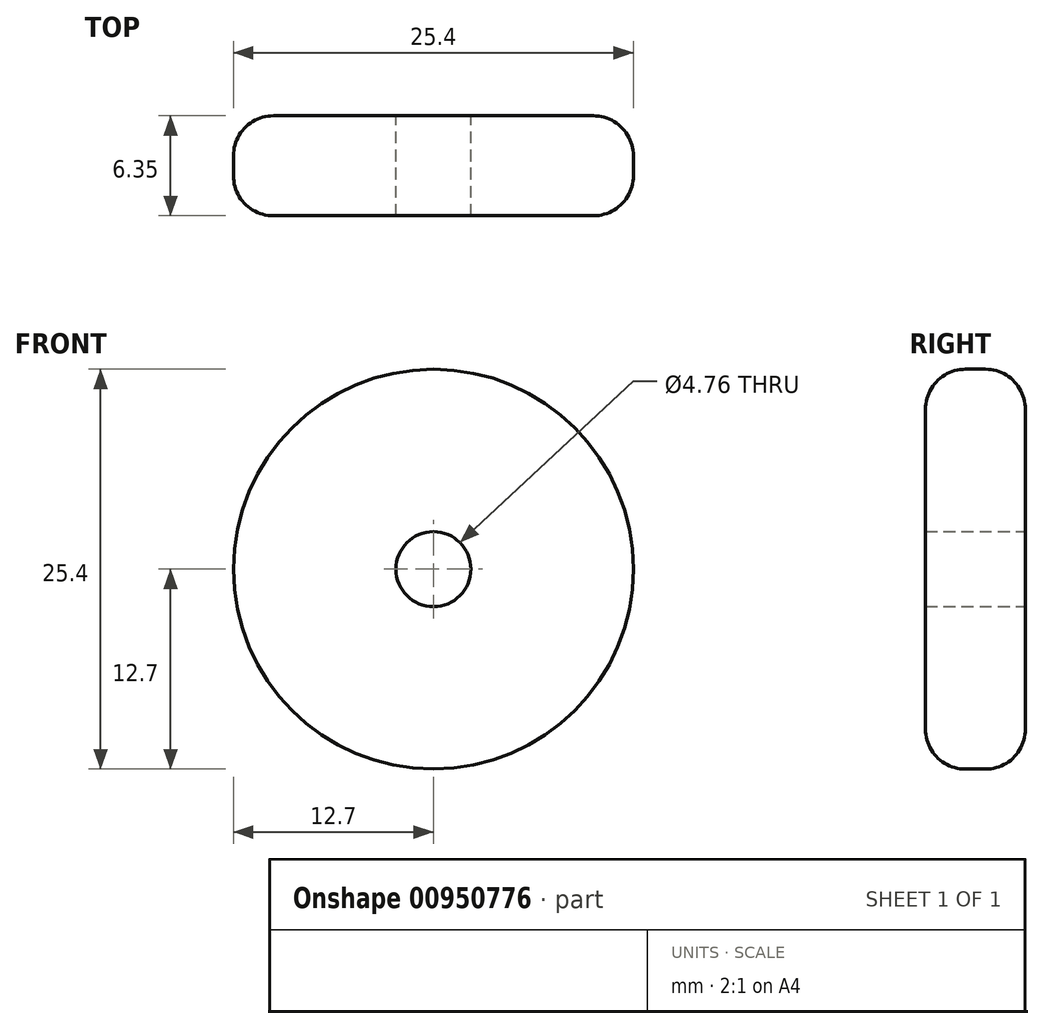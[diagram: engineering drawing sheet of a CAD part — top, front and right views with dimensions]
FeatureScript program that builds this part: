
annotation { "Feature Type Name" : "Feature", "Feature Type Description" : "" }
export const myFeature = defineFeature(function(context is Context, id is Id, definition is map)
    precondition{}
    {
        {
            var Q0;
            Q0=qCreatedBy(makeId("Front.planeOp"),FACE);
            var sketch = newSketch(context, id + "F0", { "sketchPlane" : qUnion([Q0])});
            skPoint(sketch, "E0", {"position": v(0, 0) * mm});
            skLineSegment(sketch, "E1", {"start": v(0, 0) * mm, "end": v(-12.7, 0) * mm});
            skCircle(sketch, "E2", {"center": v(0, 0) * mm, "radius": 12.7 * mm});
            skLineSegment(sketch, "E3", {"start": v(0, 0) * mm, "end": v(0, -2.38) * mm});
            skCircle(sketch, "E4", {"center": v(0, 0) * mm, "radius": 2.38 * mm});
            skSolve(sketch);
        }
        {
            var Q0;
            Q0=makeQuery(id+"F0.imprint","IMPRINT",FACE,{"disambiguationData":[TD([[makeQuery(id+"F0.imprint","IMPRINT",EDGE,{"derivedFrom":sQuery(id+"F0.wireOp",EDGE,"E2")}),1.0]])]});
            extrude(context, id + "F1", {"entities" : qUnion([Q0]), "depth" : 6.35 * mm, "offsetDistance" : 25.4 * mm});
        }
        {
            var Q0;
            Q0=makeQuery(id+"F1.opExtrude","CAP_EDGE",EDGE,{"disambiguationData":[OSD([sQuery(id+"F0.wireOp",EDGE,"E2")])],"isStart":false});
            var Q1;
            Q1=makeQuery(id+"F1.opExtrude","CAP_EDGE",EDGE,{"disambiguationData":[OSD([sQuery(id+"F0.wireOp",EDGE,"E2")])],"isStart":true});
            fillet(context, id + "F2", {"entities" : qUnion([Q0, Q1]), "radius" : 2.54 * mm, "tangentPropagation" : true, "allowEdgeOverflow" : false});
        }
    });
